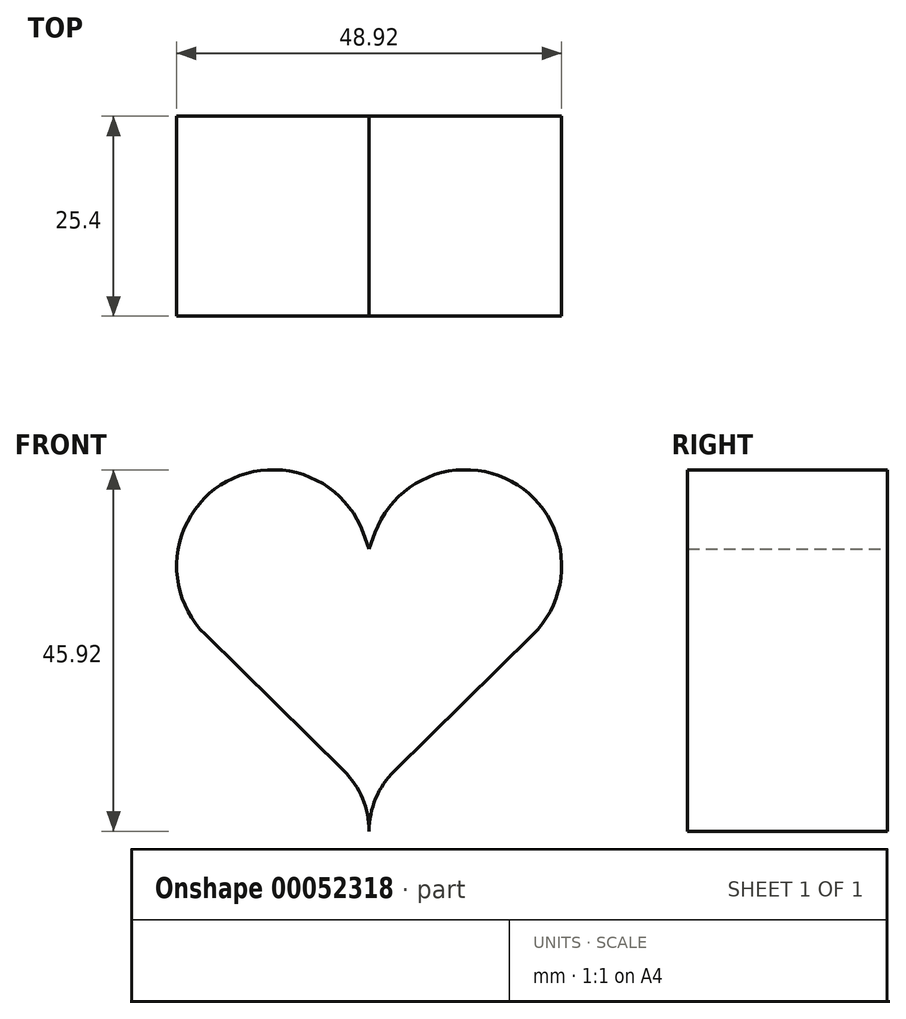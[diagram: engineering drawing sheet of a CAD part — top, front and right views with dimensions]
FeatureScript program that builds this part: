
annotation { "Feature Type Name" : "Feature", "Feature Type Description" : "" }
export const myFeature = defineFeature(function(context is Context, id is Id, definition is map)
    precondition{}
    {
        {
            var Q0;
            Q0=qCreatedBy(makeId("Front.planeOp"),FACE);
            var sketch = newSketch(context, id + "F0", { "sketchPlane" : qUnion([Q0])});
            skArc(sketch, "E0", {"start": v(-0.76, 23.77) * mm, "mid": v(-18.87, 29.8) * mm, "end": v(-20.8, 10.8) * mm});
            skArc(sketch, "E1", {"start": v(20.8, 10.8) * mm, "mid": v(18.87, 29.8) * mm, "end": v(0.76, 23.77) * mm});
            skLineSegment(sketch, "E2", {"start": v(-20.8, 10.8) * mm, "end": v(-3.2, -6.53) * mm});
            skLineSegment(sketch, "E3", {"start": v(20.8, 10.8) * mm, "end": v(3.2, -6.53) * mm});
            skArc(sketch, "E4", {"start": v(0, -14.17) * mm, "mid": v(-0.83, -10.03) * mm, "end": v(-3.2, -6.53) * mm});
            skArc(sketch, "E5", {"start": v(3.2, -6.53) * mm, "mid": v(0.83, -10.03) * mm, "end": v(0, -14.17) * mm});
            skLineSegment(sketch, "E6", {"start": v(-0.76, 23.77) * mm, "end": v(0, 21.71) * mm});
            skLineSegment(sketch, "E7", {"start": v(0, 21.71) * mm, "end": v(0.76, 23.77) * mm});
            skSolve(sketch);
        }
        {
            var Q0;
            Q0 = qSketchRegion(id + "F0", true);
            extrude(context, id + "F1", {"entities" : qUnion([Q0]), "depth" : 25.4 * mm});
        }
    });
